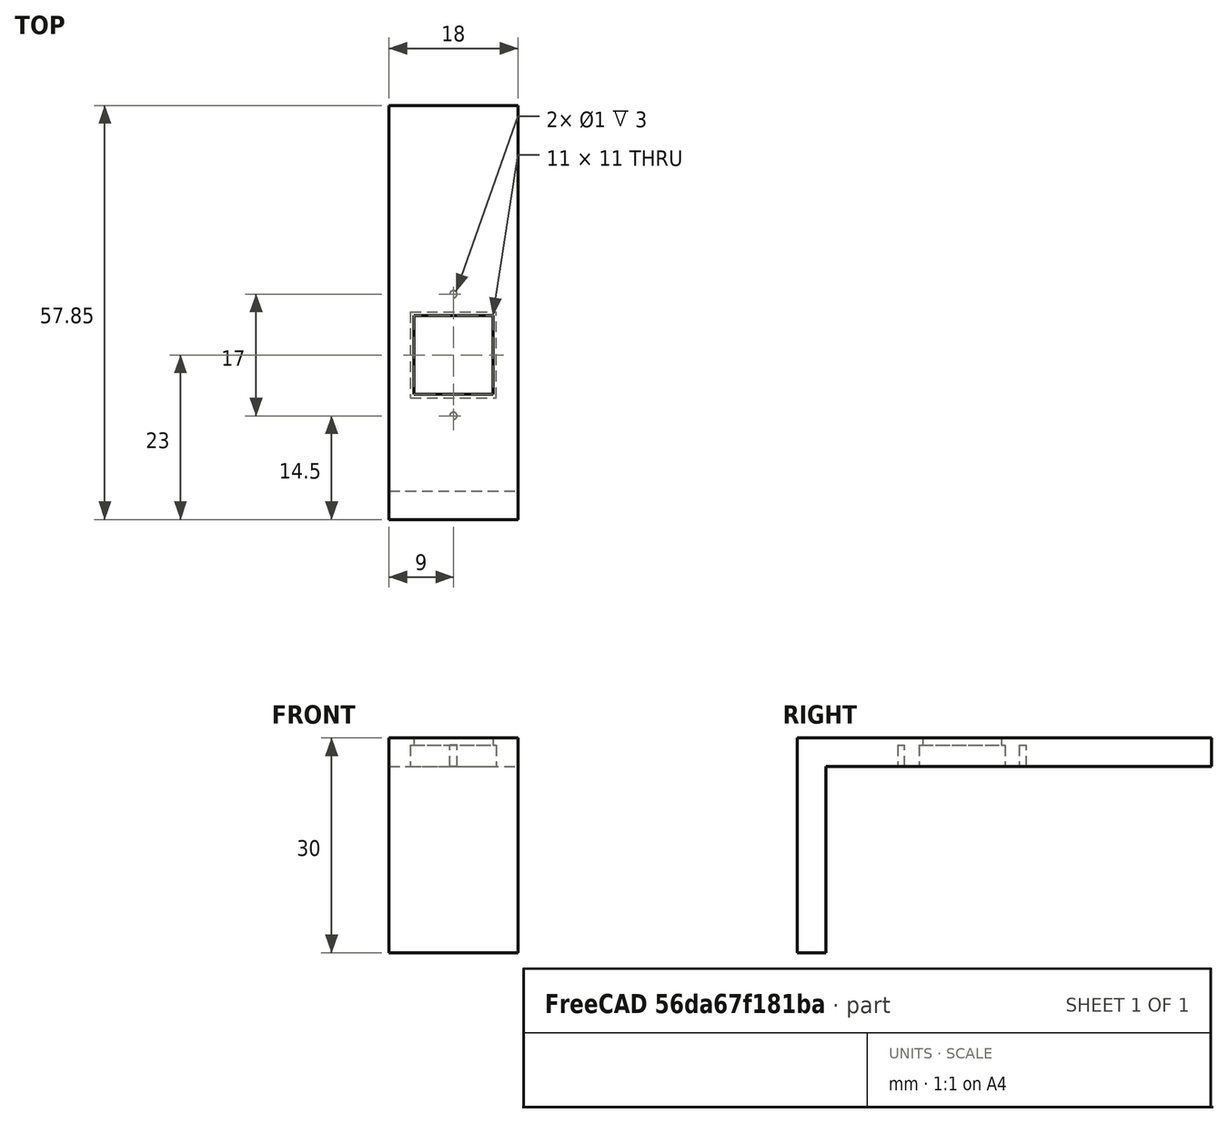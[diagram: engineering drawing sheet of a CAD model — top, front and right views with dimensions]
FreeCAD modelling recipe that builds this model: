
FCSTD DOCUMENT  (FreeCAD 0.17R13522 (Git))
Label: panel_boton
License: CreativeCommons Attribution-ShareAlike
LicenseURL: http://creativecommons.org/licenses/by-sa/4.0/
objects: Part::Cut×35, Part::Feature×30, Part::Box×10, Part::Fuse×8, Part::Cylinder×2
note: 85 computed .brp shape members not serialized (recipe doc carries the construction recipe); baked Part::Feature solids carry a one-line shape summary decoded from their .brp

FEATURE [Part::Box] Box001  label="Cube"
  AttacherType = Attacher::AttachEngine3D
  Height = 3
  Length = 6
  Placement = pos=(39,81,-108) rot=(0,0,1;0rad)
  Width = 6
FEATURE [Part::Feature] Fusion008001001061001  label="panel_siplays_encoders_dobles_y_spacers"
  Placement = pos=(0,0,-105) rot=(0,0,1;0rad)
  shape: bbox 280 x 210 x 10 mm, 411 faces (baked)
FEATURE [Part::Feature] Fusion003002001  label="el perforador001"
  Placement = pos=(48,115,-108) rot=(0,1,0;3.14159rad)
  shape: bbox 22 x 12 x 18 mm, 19 faces (baked)
FEATURE [Part::Feature] Fusion003002001001  label="el perforador002"
  Placement = pos=(87.5,115,-108) rot=(0,1,0;3.14159rad)
  shape: bbox 22 x 12 x 18 mm, 19 faces (baked)
FEATURE [Part::Cut] Cut001001001002003001008002002004
  Base = -> Fusion008001001061001
  Refine = true
  Tool = -> Fusion003002001
FEATURE [Part::Feature] Fusion003002001001001  label="el perforador003"
  Placement = pos=(127,115,-108) rot=(0,1,0;3.14159rad)
  shape: bbox 22 x 12 x 18 mm, 19 faces (baked)
FEATURE [Part::Cut] Cut001001001002003001008002002005
  Base = -> Cut001001001002003001008002002004
  Refine = true
  Tool = -> Fusion003002001001
FEATURE [Part::Feature] Fusion003002001001001001  label="el perforador004"
  Placement = pos=(166.5,115,-108) rot=(0,1,0;3.14159rad)
  shape: bbox 22 x 12 x 18 mm, 19 faces (baked)
FEATURE [Part::Feature] Fusion003002001001001001001  label="el perforador005"
  Placement = pos=(206,115,-108) rot=(0,1,0;3.14159rad)
  shape: bbox 22 x 12 x 18 mm, 19 faces (baked)
FEATURE [Part::Cut] Cut001001001002003001008002002006
  Base = -> Cut001001001002003001008002002005
  Refine = true
  Tool = -> Fusion003002001001001001
FEATURE [Part::Cut] Cut001001001002003001008002002007
  Base = -> Cut001001001002003001008002002006
  Refine = true
  Tool = -> Fusion003002001001001001001
FEATURE [Part::Feature] Fusion003002001001001001002001001  label="el perforador008"
  Placement = pos=(127,40,-108) rot=(0,1,0;3.14159rad)
  shape: bbox 22 x 12 x 18 mm, 19 faces (baked)
FEATURE [Part::Feature] Fusion003002001001001001002001002  label="el perforador009"
  Placement = pos=(127,80.5,-108) rot=(0,1,0;3.14159rad)
  shape: bbox 22 x 12 x 18 mm, 19 faces (baked)
FEATURE [Part::Feature] Fusion003002001001001001002001  label="el perforador007"
  Placement = pos=(127,55,-108) rot=(0,1,0;3.14159rad)
  shape: bbox 22 x 12 x 18 mm, 19 faces (baked)
FEATURE [Part::Feature] Fusion003002001001001001002  label="el perforador006"
  Placement = pos=(127,95.5,-108) rot=(0,1,0;3.14159rad)
  shape: bbox 22 x 12 x 18 mm, 19 faces (baked)
FEATURE [Part::Cut] Cut001001001002003001008002002008
  Base = -> Cut001001001002003001008002002007
  Refine = true
  Tool = -> Fusion003002001001001
FEATURE [Part::Cut] Cut001001001002003001008002002009
  Base = -> Cut001001001002003001008002002008
  Refine = true
  Tool = -> Fusion003002001001001001002
FEATURE [Part::Cut] Cut001001001002003001008002002010
  Base = -> Cut001001001002003001008002002009
  Refine = true
  Tool = -> Fusion003002001001001001002001
FEATURE [Part::Box] Box001001002002002001003001001004001001001001001001002  label="Cube034"
  AttacherType = Attacher::AttachEngine3D
  Height = 4
  Length = 32
  Placement = pos=(200,15,-108) rot=(0,0,1;0rad)
  Width = 10
FEATURE [Part::Fuse] Fusion003002001001001001002001003
  Base = -> Cut001001001002003001008002002010
  Refine = true
  Tool = -> Box001001002002002001003001001004001001001001001001002
FEATURE [Part::Fuse] Fusion003002001001001001002001004
  Base = -> Box001001002002002001003001001004001001001001001001002
  Refine = true
  Tool = -> Fusion003002001001001001002001003
FEATURE [Part::Fuse] Fusion003002001001001001002001005
  Refine = true
  Tool = -> Fusion003002001001001001002001004
FEATURE [Part::Fuse] Fusion003002001001001001002001006
  Base = -> Box001
  Refine = true
  Tool = -> Fusion003002001001001001002001005
FEATURE [Part::Feature] Fusion003002001001001001002001002001  label="el perforador010"
  Placement = pos=(47,80.5,-108) rot=(0,1,0;3.14159rad)
  shape: bbox 22 x 12 x 18 mm, 19 faces (baked)
FEATURE [Part::Feature] Fusion003002001001001001002001002002  label="el perforador011"
  Placement = pos=(87,80.5,-108) rot=(0,1,0;3.14159rad)
  shape: bbox 22 x 12 x 18 mm, 19 faces (baked)
FEATURE [Part::Feature] Fusion003002001001001001002001001001  label="el perforador012"
  Placement = pos=(87,40,-108) rot=(0,1,0;3.14159rad)
  shape: bbox 22 x 12 x 18 mm, 19 faces (baked)
FEATURE [Part::Feature] Fusion003002001001001001002001001001001  label="el perforador013"
  Placement = pos=(47,40,-108) rot=(0,1,0;3.14159rad)
  shape: bbox 22 x 12 x 18 mm, 19 faces (baked)
FEATURE [Part::Cut] Cut001001001002003001008002002011
  Base = -> Fusion003002001001001001002001006
  Refine = true
  Tool = -> Fusion003002001001001001002001002
FEATURE [Part::Cut] Cut001001001002003001008002002012
  Base = -> Cut001001001002003001008002002011
  Refine = true
  Tool = -> Fusion003002001001001001002001002002
FEATURE [Part::Cut] Cut001001001002003001008002002013
  Base = -> Cut001001001002003001008002002012
  Refine = true
  Tool = -> Fusion003002001001001001002001002001
FEATURE [Part::Cut] Cut001001001002003001008002002014
  Base = -> Cut001001001002003001008002002013
  Refine = true
  Tool = -> Fusion003002001001001001002001001001001
FEATURE [Part::Feature] Fusion003002001001001001002001001001002  label="el perforador014"
  Placement = pos=(220,8,-108) rot=(0.707107,0.707107,0;3.14159rad)
  shape: bbox 12 x 22 x 18 mm, 19 faces (baked)
FEATURE [Part::Cut] Cut001001001002003001008002002015
  Base = -> Cut001001001002003001008002002014
  Refine = true
  Tool = -> Fusion003002001001001001002001001001
FEATURE [Part::Cut] Cut001001001002003001008002002016
  Base = -> Cut001001001002003001008002002015
  Refine = true
  Tool = -> Fusion003002001001001001002001001
FEATURE [Part::Cut] Cut001001001002003001008002002017  label="base solo faltan los leds"
  Base = -> Cut001001001002003001008002002016
  Refine = true
  Tool = -> Fusion003002001001001001002001001001002
FEATURE [Part::Feature] Fusion001001  label="perforador led 3 mm001 rojo com2"
  Placement = pos=(24,43,-108) rot=(0,1,0;3.14159rad)
  shape: bbox 6 x 6 x 10 mm, 13 faces (baked)
FEATURE [Part::Feature] Fusion003002001001001001002001001001003  label="perforador led 3 mm002 rojo nav2"
  Placement = pos=(61,43,-108) rot=(0,1,0;3.14159rad)
  shape: bbox 6 x 6 x 10 mm, 13 faces (baked)
FEATURE [Part::Feature] Fusion003002001001001001002001001001004  label="perforador led 3 mm002 rojo adf2"
  Placement = pos=(101,43,-108) rot=(0,1,0;3.14159rad)
  shape: bbox 6 x 6 x 10 mm, 13 faces (baked)
FEATURE [Part::Feature] Fusion003002001001001001002001001001005  label="perforador led 3 mm001 rojo com1"
  Placement = pos=(24,83.5,-108) rot=(0,1,0;3.14159rad)
  shape: bbox 6 x 6 x 10 mm, 13 faces (baked)
FEATURE [Part::Feature] Fusion003002001001001001002001001001006  label="perforador led 3 mm002 rojo nav1"
  Placement = pos=(61,83.5,-108) rot=(0,1,0;3.14159rad)
  shape: bbox 6 x 6 x 10 mm, 13 faces (baked)
FEATURE [Part::Feature] Fusion003002001001001001002001001001007  label="perforador led 3 mm002 rojo adf1"
  Placement = pos=(101,83.5,-108) rot=(0,1,0;3.14159rad)
  shape: bbox 6 x 6 x 10 mm, 13 faces (baked)
FEATURE [Part::Cut] Cut
  Base = -> Cut001001001002003001008002002017
  Refine = true
  Tool = -> Fusion003002001001001001002001001001005
FEATURE [Part::Cut] Cut001001001002003001008002002018
  Base = -> Cut
  Refine = true
  Tool = -> Fusion003002001001001001002001001001006
FEATURE [Part::Cut] Cut001001001002003001008002002019
  Base = -> Cut001001001002003001008002002018
  Refine = true
  Tool = -> Fusion003002001001001001002001001001007
FEATURE [Part::Cut] Cut001001001002003001008002002020
  Base = -> Cut001001001002003001008002002019
  Refine = true
  Tool = -> Fusion003002001001001001002001001001004
FEATURE [Part::Cut] Cut001001001002003001008002002021
  Base = -> Cut001001001002003001008002002020
  Refine = true
  Tool = -> Fusion003002001001001001002001001001003
FEATURE [Part::Cut] Cut001001001002003001008002002022
  Base = -> Cut001001001002003001008002002021
  Refine = true
  Tool = -> Fusion001001
FEATURE [Part::Feature] Fusion003002001001001001002001001001008  label="perforador led 5 mm sound marker"
  Placement = pos=(40.75,133,-108) rot=(0,1,0;3.14159rad)
  shape: bbox 7.5 x 7.5 x 10 mm, 13 faces (baked)
FEATURE [Part::Feature] Fusion003002001001001001002001001001009  label="perforador led 5 mm sound com1"
  Placement = pos=(80.25,133,-108) rot=(0,1,0;3.14159rad)
  shape: bbox 7.5 x 7.5 x 10 mm, 13 faces (baked)
FEATURE [Part::Feature] Fusion003002001001001001002001001001010  label="perforador led 5 mm sound nav1"
  Placement = pos=(119.75,133,-108) rot=(0,1,0;3.14159rad)
  shape: bbox 7.5 x 7.5 x 10 mm, 13 faces (baked)
FEATURE [Part::Feature] Fusion003002001001001001002001001001011  label="perforador led 5 mm sound dme"
  Placement = pos=(159.25,133,-108) rot=(0,1,0;3.14159rad)
  shape: bbox 7.5 x 7.5 x 10 mm, 13 faces (baked)
FEATURE [Part::Feature] Fusion003002001001001001002001001001012  label="perforador led 5 mm sound adf1"
  Placement = pos=(198.75,133,-108) rot=(0,1,0;3.14159rad)
  shape: bbox 7.5 x 7.5 x 10 mm, 13 faces (baked)
FEATURE [Part::Feature] Fusion003002001001001001002001001001013  label="perforador led 5 mm ON/OFF"
  Placement = pos=(263.5,133,-108) rot=(0,1,0;3.14159rad)
  shape: bbox 7.5 x 7.5 x 10 mm, 13 faces (baked)
FEATURE [Part::Cut] Cut001001001002003001008002002023
  Base = -> Cut001001001002003001008002002022
  Refine = true
  Tool = -> Fusion003002001001001001002001001001013
FEATURE [Part::Cut] Cut001001001002003001008002002024
  Base = -> Cut001001001002003001008002002023
  Refine = true
  Tool = -> Fusion003002001001001001002001001001012
FEATURE [Part::Cut] Cut001001001002003001008002002025
  Base = -> Cut001001001002003001008002002024
  Refine = true
  Tool = -> Fusion003002001001001001002001001001011
FEATURE [Part::Cut] Cut001001001002003001008002002026
  Base = -> Cut001001001002003001008002002025
  Refine = true
  Tool = -> Fusion003002001001001001002001001001010
FEATURE [Part::Cut] Cut001001001002003001008002002027
  Base = -> Cut001001001002003001008002002026
  Refine = true
  Tool = -> Fusion003002001001001001002001001001009
FEATURE [Part::Cut] Cut001001001002003001008002002028
  Base = -> Cut001001001002003001008002002027
  Refine = true
  Tool = -> Fusion003002001001001001002001001001008
FEATURE [Part::Box] Box  label="Cube035"
  AttacherType = Attacher::AttachEngine3D
  Height = 10
  Length = 300
  Placement = pos=(-8,153.85,-111) rot=(0,0,1;0rad)
  Width = 120
FEATURE [Part::Cut] Cut001001001002003001008002002029  label="panel sin letras"
  Base = -> Cut001001001002003001008002002028
  Refine = true
  Tool = -> Box
FEATURE [Part::Cylinder] Cylinder  label="clavija agujereadora1_1"
  Angle = 360
  AttacherType = Attacher::AttachEngine3D
  Height = 30
  Placement = pos=(115,111.85,-106) rot=(0,1,0;1.5708rad)
  Radius = 1.05
FEATURE [Part::Cylinder] Cylinder001  label="clavija agujereadora2_1"
  Angle = 360
  AttacherType = Attacher::AttachEngine3D
  Height = 30
  Placement = pos=(115,37.85,-106) rot=(0,1,0;1.5708rad)
  Radius = 1.05
FEATURE [Part::Cut] Cut001001001002003001008002002030
  Base = -> Cut001001001002003001008002002029
  Refine = true
  Tool = -> Cylinder
FEATURE [Part::Cut] Cut001001001002003001008002002031  label="panel sin letras con agujeros clavijas"
  Base = -> Cut001001001002003001008002002030
  Refine = true
  Tool = -> Cylinder001
FEATURE [Part::Box] Box001001002002002001003001001004001001001001001001006  label="fleje abajo"
  AttacherType = Attacher::AttachEngine3D
  Height = 4
  Length = 280
  Placement = pos=(0,-4,-108) rot=(0,0,1;0rad)
  Width = 4
FEATURE [Part::Fuse] Fusion
  Base = -> Cut001001001002003001008002002031
  Refine = true
  Tool = -> Box001001002002002001003001001004001001001001001001006
FEATURE [Part::Feature] Cylinder002001  label="clavija empalmadora une frente base"
  Placement = pos=(30,-2,-134) rot=(0,0,1;1.5708rad)
  shape: bbox 2 x 2 x 29.8 mm, 3 faces (baked)
FEATURE [Part::Feature] Cylinder002001001  label="clavija empalmadora une frente base2"
  Placement = pos=(250,-2,-134) rot=(0,0,1;1.5708rad)
  shape: bbox 2 x 2 x 29.8 mm, 3 faces (baked)
FEATURE [Part::Fuse] Fusion003002001001001001002001001001014
  Base = -> Fusion
  Refine = true
  Tool = -> Cylinder002001
FEATURE [Part::Fuse] Fusion003002001001001001002001001001015  label="frente con clavijas sin letras"
  Base = -> Cylinder002001001
  Refine = true
  Tool = -> Fusion003002001001001001002001001001014
FEATURE [Part::Box] Box001001002002002001003001001004001001001001001001007  label="cortador clavijas"
  AttacherType = Attacher::AttachEngine3D
  Height = 4
  Length = 280
  Placement = pos=(0,0,-153) rot=(1,0,0;1.5708rad)
  Width = 30
FEATURE [Part::Cut] Cut001001001002003001008002002032  label="frente con clavijas de 15 sin letras"
  Base = -> Fusion003002001001001001002001001001015
  Refine = true
  Tool = -> Box001001002002002001003001001004001001001001001001007
FEATURE [Part::Box] Box001001002002002001003001001004001001001001001001008  label="Cube036"
  AttacherType = Attacher::AttachEngine3D
  Height = 60
  Length = 250
  Placement = pos=(-33,-26,-133) rot=(0,0,1;0rad)
  Width = 200
FEATURE [Part::Cut] Cut001001001002003001008002002033
  Base = -> Cut001001001002003001008002002032
  Refine = true
  Tool = -> Box001001002002002001003001001004001001001001001001008
FEATURE [Part::Box] Box001001002002002001003001001004001001001001001001009  label="Cube037"
  AttacherType = Attacher::AttachEngine3D
  Height = 60
  Length = 100
  Placement = pos=(235,-27,-134) rot=(0,0,1;0rad)
  Width = 200
FEATURE [Part::Cut] Cut001001001002003001008002002034
  Base = -> Cut001001001002003001008002002033
  Refine = true
  Tool = -> Box001001002002002001003001001004001001001001001001009
FEATURE [Part::Box] Box001001002002002001003001001004001001001001001001010  label="Cube038"
  AttacherType = Attacher::AttachEngine3D
  Height = 27
  Length = 33
  Placement = pos=(209,53.85,-118) rot=(0,0,1;0rad)
  Width = 150
FEATURE [Part::Cut] Cut001001001002003001008002002035
  Base = -> Cut001001001002003001008002002034
  Refine = true
  Tool = -> Box001001002002002001003001001004001001001001001001010
FEATURE [Part::Box] Box001001002002002001003001001004001001001001001001011  label="Cube039"
  AttacherType = Attacher::AttachEngine3D
  Height = 30
  Length = 22
  Placement = pos=(215,-4,-134) rot=(0,0,1;0rad)
  Width = 4
FEATURE [Part::Fuse] Fusion003002001001001001002001001001016
  Base = -> Cut001001001002003001008002002035
  Refine = true
  Tool = -> Box001001002002002001003001001004001001001001001001011
FEATURE [Part::Box] Box001001002002002001003001001004001001001001001001012  label="Cube040"
  AttacherType = Attacher::AttachEngine3D
  Height = 39
  Length = 8
  Placement = pos=(235,-10,-143) rot=(0,0,1;0rad)
  Width = 10
FEATURE [Part::Feature] Box001001002002002001003001001004001001001001001001012001  label="Cube041"
  Placement = pos=(209,-10,-143) rot=(0,0,1;0rad)
  shape: bbox 8 x 10 x 39 mm, 6 faces (baked)
FEATURE [Part::Cut] Cut001001001002003001008002002036
  Base = -> Fusion003002001001001001002001001001016
  Refine = true
  Tool = -> Box001001002002002001003001001004001001001001001001012001
FEATURE [Part::Cut] Cut001001001002003001008002002037
  Base = -> Cut001001001002003001008002002036
  Refine = true
  Tool = -> Box001001002002002001003001001004001001001001001001012
